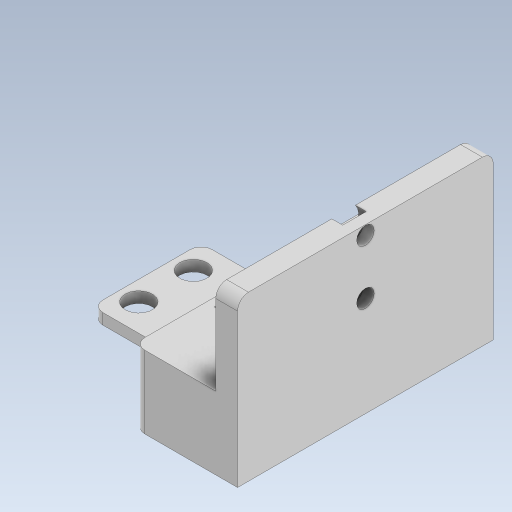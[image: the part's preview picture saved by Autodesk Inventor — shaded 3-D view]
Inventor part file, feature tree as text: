
AUTODESK INVENTOR PART (.ipt)
format: ipt  version: 2023.5 (Build 275446000, 446)  size: 421,888 bytes
history: native  units: mm
features: extrude x6, sketch x2, fillet x2
ambient origin geometry x8: Origin, YZ Plane, XZ Plane, XY Plane, X Axis, Y Axis, Z Axis, Center Point
bodies: Solid1 (feature_tree)
feature tree (10):
  sketch  "Sketch1"  dims[d2=12.0mm d3=22.875mm]
  extrude  "Extrusion1"  Depth=22.875mm
  extrude  "Extrusion2"  Depth=32.3mm
  extrude  "Extrusion3"  Depth=10.0mm
  fillet  "Fillet1"  Radius=6.0mm
  extrude  "Extrusion4"  Depth=10.0mm
  sketch  "Sketch2"  dims[d4=12.0mm d5=32.3mm d6=5.0mm d7=6.0mm d8=5.0mm d9=22.8mm d10=15.0mm d11=35.0mm d12=10.8mm d13=0.0mm d14=13.3mm d15=0.0mm d17=5.0mm d18=15.0mm d19=6.4mm d20=5.0mm d21=10.0mm d22=5.0mm d23=10.0mm d25=5.0mm d27=10.0mm d28=2.0mm d29=0.0mm d30=2.0mm d31=4.0mm d32=30.0mm d33=0.0mm d34=3.2mm d35=5.5mm d36=3.2mm d37=5.5mm d39=5.0mm d40=10.0mm d41=4.0mm d42=0.0mm d43=2.0mm d44=0.0mm d45=2.0mm d46=10.0mm]
  extrude  "Extrusion5"  Depth=10.0mm
  extrude  "Extrusion6"  Depth=15.0mm
  fillet  "Fillet2"  Radius=35.0mm
